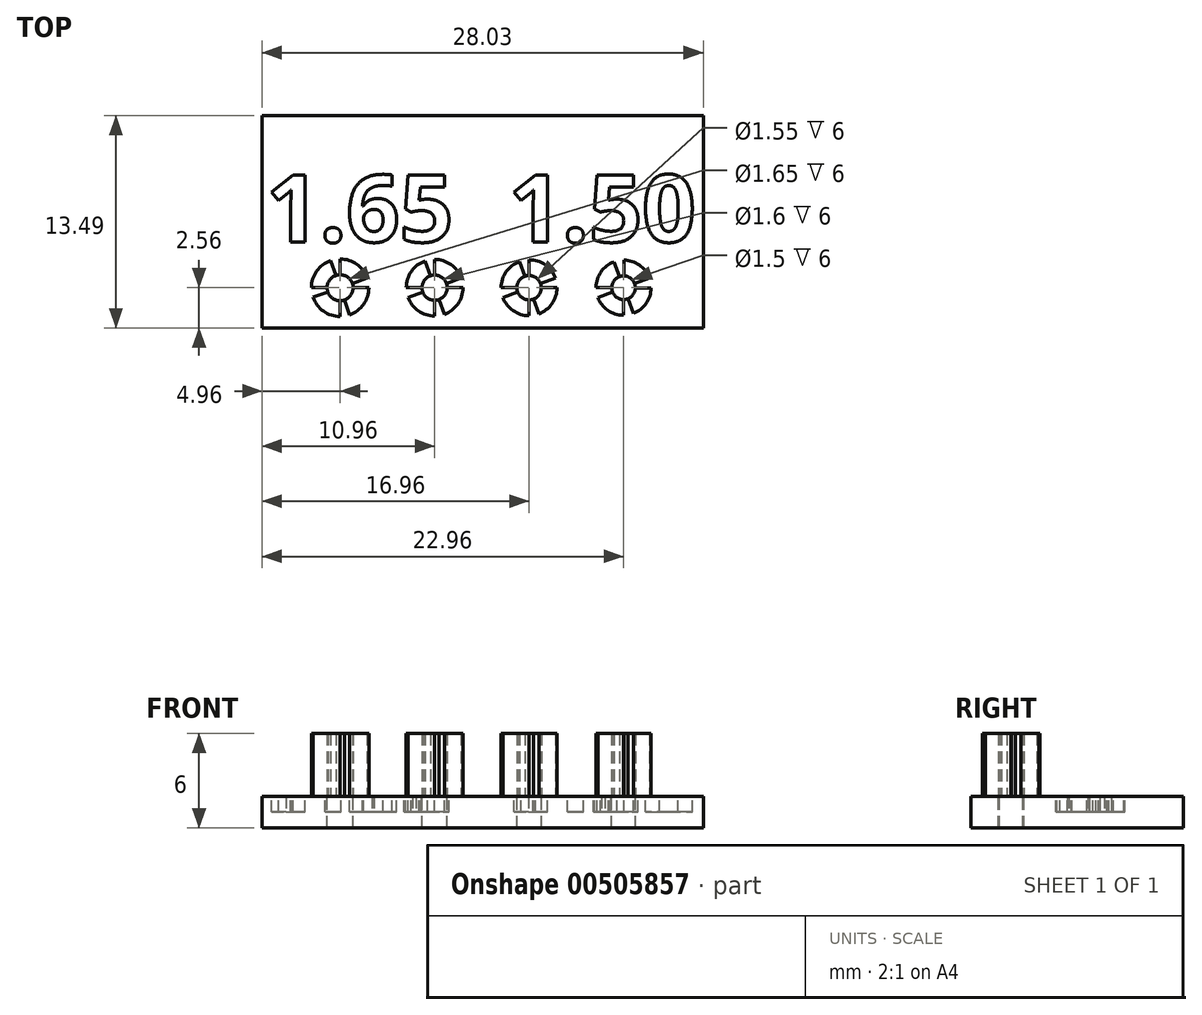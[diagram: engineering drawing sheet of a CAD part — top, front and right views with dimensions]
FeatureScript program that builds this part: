
annotation { "Feature Type Name" : "Feature", "Feature Type Description" : "" }
export const myFeature = defineFeature(function(context is Context, id is Id, definition is map)
    precondition{}
    {
        {
            var Q0;
            Q0=qCreatedBy(makeId("Top.planeOp"),FACE);
            var sketch = newSketch(context, id + "F0", { "sketchPlane" : qUnion([Q0])});
            skArc(sketch, "E0", {"start": v(0, 0.8) * mm, "mid": v(0.46, 0.66) * mm, "end": v(0.75, 0.27) * mm});
            skLineSegment(sketch, "E1", {"start": v(0, 0.8) * mm, "end": v(0, 0) * mm, "construction": true});
            skLineSegment(sketch, "E2", {"start": v(0, 0) * mm, "end": v(0.75, 0.27) * mm, "construction": true});
            skArc(sketch, "E3.0", {"start": v(0, 1.8) * mm, "mid": v(1.03, 1.47) * mm, "end": v(1.7, 0.62) * mm});
            skLineSegment(sketch, "E4", {"start": v(0.75, 0.27) * mm, "end": v(1.7, 0.62) * mm});
            skLineSegment(sketch, "E5", {"start": v(0, 0.8) * mm, "end": v(0, 1.8) * mm});
            skArc(sketch, "E6", {"start": v(6, 0.77) * mm, "mid": v(6.44, 0.64) * mm, "end": v(6.73, 0.27) * mm});
            skArc(sketch, "E7.0", {"start": v(6, 1.77) * mm, "mid": v(7.01, 1.46) * mm, "end": v(7.66, 0.62) * mm});
            skLineSegment(sketch, "E8", {"start": v(6, 0.77) * mm, "end": v(6, 1.77) * mm});
            skLineSegment(sketch, "E9", {"start": v(6.73, 0.27) * mm, "end": v(7.66, 0.62) * mm});
            skArc(sketch, "E10", {"start": v(12.02, 0.75) * mm, "mid": v(12.43, 0.61) * mm, "end": v(12.7, 0.27) * mm});
            skLineSegment(sketch, "E11", {"start": v(0, 0) * mm, "end": v(6, 0) * mm, "construction": true});
            skLineSegment(sketch, "E12", {"start": v(6, 0) * mm, "end": v(12, 0) * mm, "construction": true});
            skLineSegment(sketch, "E13", {"start": v(12.02, 0.75) * mm, "end": v(12.02, 1.75) * mm});
            skLineSegment(sketch, "E14", {"start": v(12.7, 0.27) * mm, "end": v(13.64, 0.62) * mm});
            skArc(sketch, "E15", {"start": v(12.02, 1.75) * mm, "mid": v(13, 1.43) * mm, "end": v(13.64, 0.62) * mm});
            skArc(sketch, "E16", {"start": v(-6, 0.82) * mm, "mid": v(-5.52, 0.67) * mm, "end": v(-5.22, 0.27) * mm});
            skLineSegment(sketch, "E17", {"start": v(-6, 0) * mm, "end": v(0, 0) * mm, "construction": true});
            skLineSegment(sketch, "E18", {"start": v(-6, 0.82) * mm, "end": v(-6, 1.82) * mm});
            skLineSegment(sketch, "E19", {"start": v(-5.22, 0.27) * mm, "end": v(-4.28, 0.6) * mm});
            skArc(sketch, "E20", {"start": v(-6, 1.82) * mm, "mid": v(-4.95, 1.49) * mm, "end": v(-4.28, 0.6) * mm});
            skSolve(sketch);
        }
        {
            var Q0;
            Q0=qCreatedBy(makeId("Top.planeOp"),FACE);
            var sketch = newSketch(context, id + "F1", { "sketchPlane" : qUnion([Q0])});
            skLineSegment(sketch, "E21.bottom", {"start": v(17.07, 10.93) * mm, "end": v(-10.96, 10.93) * mm});
            skLineSegment(sketch, "E21.top", {"start": v(17.07, -2.56) * mm, "end": v(-10.96, -2.56) * mm});
            skLineSegment(sketch, "E21.left", {"start": v(17.07, 10.93) * mm, "end": v(17.07, -2.56) * mm});
            skLineSegment(sketch, "E21.right", {"start": v(-10.96, 10.93) * mm, "end": v(-10.96, -2.56) * mm});
            skCircle(sketch, "E22", {"center": v(0, 0) * mm, "radius": 0.8 * mm});
            skCircle(sketch, "E23", {"center": v(-6, 0) * mm, "radius": 0.82 * mm});
            skCircle(sketch, "E24", {"center": v(6, 0) * mm, "radius": 0.78 * mm});
            skCircle(sketch, "E25", {"center": v(12, 0) * mm, "radius": 0.75 * mm});
            skLineSegment(sketch, "E26", {"start": v(3.06, 0) * mm, "end": v(3.06, -2.56) * mm, "construction": true});
            skSolve(sketch);
        }
        {
            var Q0;
            Q0 = qSketchRegion(id + "F1", true);
            extrude(context, id + "F2", {"entities" : qUnion([Q0]), "oppositeDirection" : true, "depth" : 2 * mm});
        }
        {
            var Q0;
            Q0 = qSketchRegion(id + "F0", true);
            extrude(context, id + "F3", {"entities" : qUnion([Q0]), "depth" : 4 * mm});
        }
        {
            var Q0;
            Q0=qCreatedBy(makeId("Front.planeOp"),FACE);
            var sketch = newSketch(context, id + "F4", { "sketchPlane" : qUnion([Q0])});
            skLineSegment(sketch, "E27", {"start": v(0, 0) * mm, "end": v(0, 5.15) * mm, "construction": true});
            skLineSegment(sketch, "E28", {"start": v(6, 5.2) * mm, "end": v(6, 0) * mm, "construction": true});
            skLineSegment(sketch, "E29", {"start": v(12, 0) * mm, "end": v(12, 5.09) * mm, "construction": true});
            skLineSegment(sketch, "E30", {"start": v(-6, 0) * mm, "end": v(-6, 5.1) * mm, "construction": true});
            skSolve(sketch);
        }
        {
            var Q0;
            Q0=makeQuery(id+"F3.opExtrude","SWEPT_BODY",BODY,{"disambiguationData":[OSD([sQuery(id+"F0.wireOp",EDGE,"E10"),sQuery(id+"F0.wireOp",EDGE,"E13"),sQuery(id+"F0.wireOp",EDGE,"E14"),sQuery(id+"F0.wireOp",EDGE,"E15")])]});
            var Q1;
            Q1=sQuery(id+"F4.wireOp",EDGE,"E29");
            circularPattern(context, id + "F5", {"operationType" : NewBodyOperationType.ADD, "entities" : qUnion([Q0]), "axis" : qUnion([Q1]), "angle" : 360 * degree, "instanceCount" : 4, "equalSpace" : true});
        }
        {
            var Q0;
            Q0=makeQuery(id+"F3.opExtrude","SWEPT_BODY",BODY,{"disambiguationData":[OSD([sQuery(id+"F0.wireOp",EDGE,"E6"),sQuery(id+"F0.wireOp",EDGE,"E7.0"),sQuery(id+"F0.wireOp",EDGE,"E8"),sQuery(id+"F0.wireOp",EDGE,"E9")])]});
            var Q1;
            Q1=sQuery(id+"F4.wireOp",EDGE,"E28");
            circularPattern(context, id + "F6", {"operationType" : NewBodyOperationType.ADD, "entities" : qUnion([Q0]), "axis" : qUnion([Q1]), "angle" : 360 * degree, "instanceCount" : 4, "equalSpace" : true});
        }
        {
            var Q0;
            Q0=makeQuery(id+"F3.opExtrude","SWEPT_BODY",BODY,{"disambiguationData":[OSD([sQuery(id+"F0.wireOp",EDGE,"E0"),sQuery(id+"F0.wireOp",EDGE,"E3.0"),sQuery(id+"F0.wireOp",EDGE,"E4"),sQuery(id+"F0.wireOp",EDGE,"E5")])]});
            var Q1;
            Q1=sQuery(id+"F4.wireOp",EDGE,"E27");
            circularPattern(context, id + "F7", {"operationType" : NewBodyOperationType.ADD, "entities" : qUnion([Q0]), "axis" : qUnion([Q1]), "angle" : 360 * degree, "instanceCount" : 4, "equalSpace" : true});
        }
        {
            var Q0;
            Q0=makeQuery(id+"F3.opExtrude","SWEPT_BODY",BODY,{"disambiguationData":[OSD([sQuery(id+"F0.wireOp",EDGE,"E16"),sQuery(id+"F0.wireOp",EDGE,"E18"),sQuery(id+"F0.wireOp",EDGE,"E19"),sQuery(id+"F0.wireOp",EDGE,"E20")])]});
            var Q1;
            Q1=sQuery(id+"F4.wireOp",EDGE,"E30");
            circularPattern(context, id + "F8", {"operationType" : NewBodyOperationType.ADD, "entities" : qUnion([Q0]), "axis" : qUnion([Q1]), "angle" : 360 * degree, "instanceCount" : 4, "equalSpace" : true});
        }
        {
            var Q0;
            Q0=makeQuery(id+"F2.opExtrude","CAP_FACE",FACE,{"disambiguationData":[OSD([sQuery(id+"F1.wireOp",EDGE,"E21.bottom"),sQuery(id+"F1.wireOp",EDGE,"E21.top"),sQuery(id+"F1.wireOp",EDGE,"E21.left"),sQuery(id+"F1.wireOp",EDGE,"E21.right"),sQuery(id+"F1.wireOp",EDGE,"E22"),sQuery(id+"F1.wireOp",EDGE,"E23"),sQuery(id+"F1.wireOp",EDGE,"E24"),sQuery(id+"F1.wireOp",EDGE,"E25")])],"isStart":true});
            var sketch = newSketch(context, id + "F9", { "sketchPlane" : qUnion([Q0])});
            skText(sketch, "E31", { "text": "1.65", "fontName": "OpenSans-Bold.ttf"});
            skText(sketch, "E32", { "text": "1.50", "fontName": "OpenSans-Bold.ttf"});
            const initialGuessF9  = {"E31": [-0.0107, 0.00291, 1, 0, 0.00428], "E32": [0.0047, 0.00291, 1, 0, 0.00428]};
            skSetInitialGuess(sketch, initialGuessF9);
            skSolve(sketch);
        }
        {
            var Q0;
            Q0 = qSketchRegion(id + "F9", true);
            extrude(context, id + "F10", {"entities" : qUnion([Q0]), "operationType" : NewBodyOperationType.REMOVE, "oppositeDirection" : true, "depth" : 1 * mm});
        }
    });
